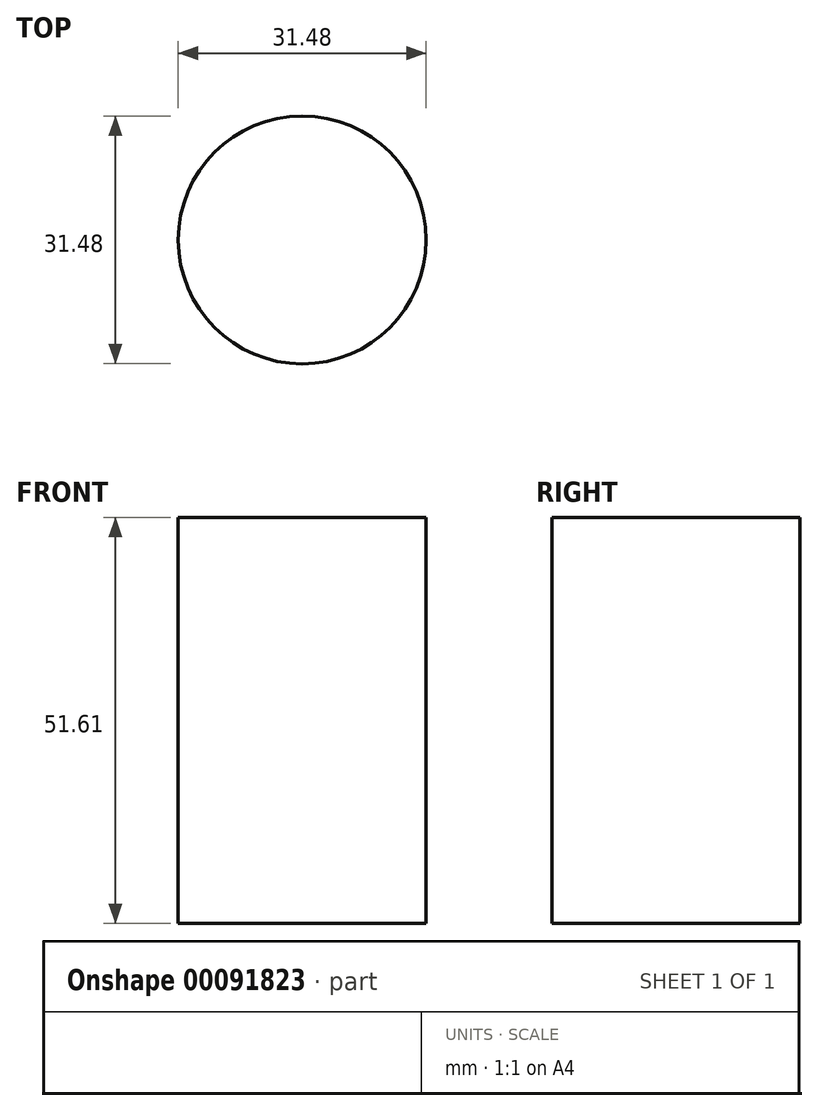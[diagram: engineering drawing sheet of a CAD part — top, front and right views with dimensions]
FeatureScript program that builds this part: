
annotation { "Feature Type Name" : "Feature", "Feature Type Description" : "" }
export const myFeature = defineFeature(function(context is Context, id is Id, definition is map)
    precondition{}
    {
        {
            var Q0;
            Q0=qCreatedBy(makeId("Top.planeOp"),FACE);
            var sketch = newSketch(context, id + "F0", { "sketchPlane" : qUnion([Q0])});
            skCircle(sketch, "E0", {"center": v(0, 0) * mm, "radius": 15.74 * mm});
            skSolve(sketch);
        }
        {
            var Q0;
            Q0 = qSketchRegion(id + "F0", true);
            extrude(context, id + "F1", {"entities" : qUnion([Q0]), "depth" : 51.6 * mm});
        }
    });
